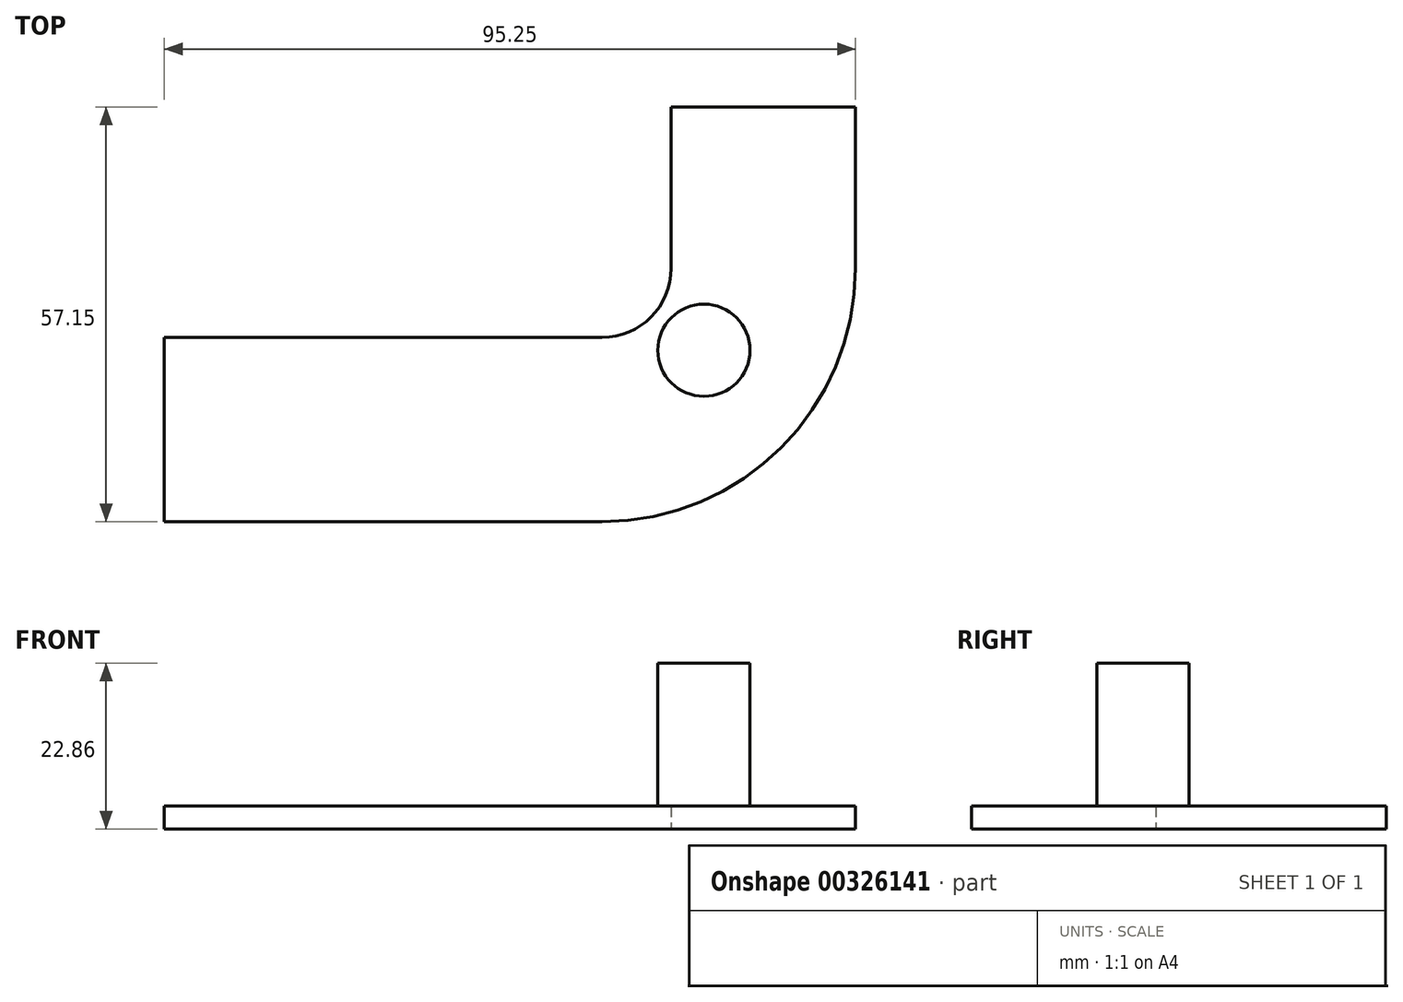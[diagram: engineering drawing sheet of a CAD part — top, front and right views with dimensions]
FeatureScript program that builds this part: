
annotation { "Feature Type Name" : "Feature", "Feature Type Description" : "" }
export const myFeature = defineFeature(function(context is Context, id is Id, definition is map)
    precondition{}
    {
        {
            var Q0;
            Q0=qCreatedBy(makeId("Top.planeOp"),FACE);
            var sketch = newSketch(context, id + "F0", { "sketchPlane" : qUnion([Q0])});
            skLineSegment(sketch, "E0", {"start": v(-25.4, 57.15) * mm, "end": v(-25.4, 34.92) * mm});
            skLineSegment(sketch, "E1", {"start": v(9.53, 0) * mm, "end": v(19.05, 0) * mm});
            skLineSegment(sketch, "E2", {"start": v(19.05, 25.4) * mm, "end": v(9.53, 25.4) * mm});
            skLineSegment(sketch, "E3", {"start": v(-25.4, 57.15) * mm, "end": v(0, 57.15) * mm});
            skLineSegment(sketch, "E4", {"start": v(0, 57.15) * mm, "end": v(0, 34.93) * mm});
            skPoint(sketch, "E5.visualSharp", {"position": v(0, 25.4) * mm});
            skArc(sketch, "E5.filletArc", {"start": v(0, 34.93) * mm, "mid": v(2.79, 28.19) * mm, "end": v(9.53, 25.4) * mm});
            skPoint(sketch, "E6.visualSharp", {"position": v(-25.4, 0) * mm});
            skArc(sketch, "E6.filletArc", {"start": v(-25.4, 34.92) * mm, "mid": v(-15.17, 10.23) * mm, "end": v(9.53, 0) * mm});
            skCircle(sketch, "E7", {"center": v(-4.5, 23.62) * mm, "radius": 6.35 * mm});
            skLineSegment(sketch, "E8", {"start": v(19.05, 0) * mm, "end": v(69.85, 0) * mm});
            skLineSegment(sketch, "E9", {"start": v(69.85, 0) * mm, "end": v(69.85, 25.4) * mm});
            skLineSegment(sketch, "E10", {"start": v(69.85, 25.4) * mm, "end": v(19.05, 25.4) * mm});
            skSolve(sketch);
        }
        {
            var Q0;
            Q0=makeQuery(id+"F0.imprint","IMPRINT",FACE,{"disambiguationData":[TD([[makeQuery(id+"F0.imprint","IMPRINT",EDGE,{"derivedFrom":sQuery(id+"F0.wireOp",EDGE,"E7")}),1.0]])]});
            extrude(context, id + "F1", {"entities" : qUnion([Q0]), "depth" : -22.86 * mm});
        }
        {
            var Q0;
            Q0=qSketchRegion(id+"F0",true);
            extrude(context, id + "F2", {"entities" : qUnion([Q0]), "operationType" : NewBodyOperationType.ADD, "depth" : -3.17 * mm});
        }
        {
            var Q0;
            Q0=makeQuery(id+"F1.opExtrude","SWEPT_BODY",BODY,{"disambiguationData":[OSD([sQuery(id+"F0.wireOp",EDGE,"E7")])]});
            var Q1;
            Q1=makeQuery(id+"F2.opExtrude","CAP_EDGE",EDGE,{"disambiguationData":[OSD([sQuery(id+"F0.wireOp",EDGE,"E4")])],"isStart":false});
            transform(context, id + "F3", {"entities" : qUnion([Q0]), "transformType" : TransformType.ROTATION, "transformAxis" : qUnion([Q1]), "angle" : 180 * degree, "makeCopy" : false});
        }
    });
